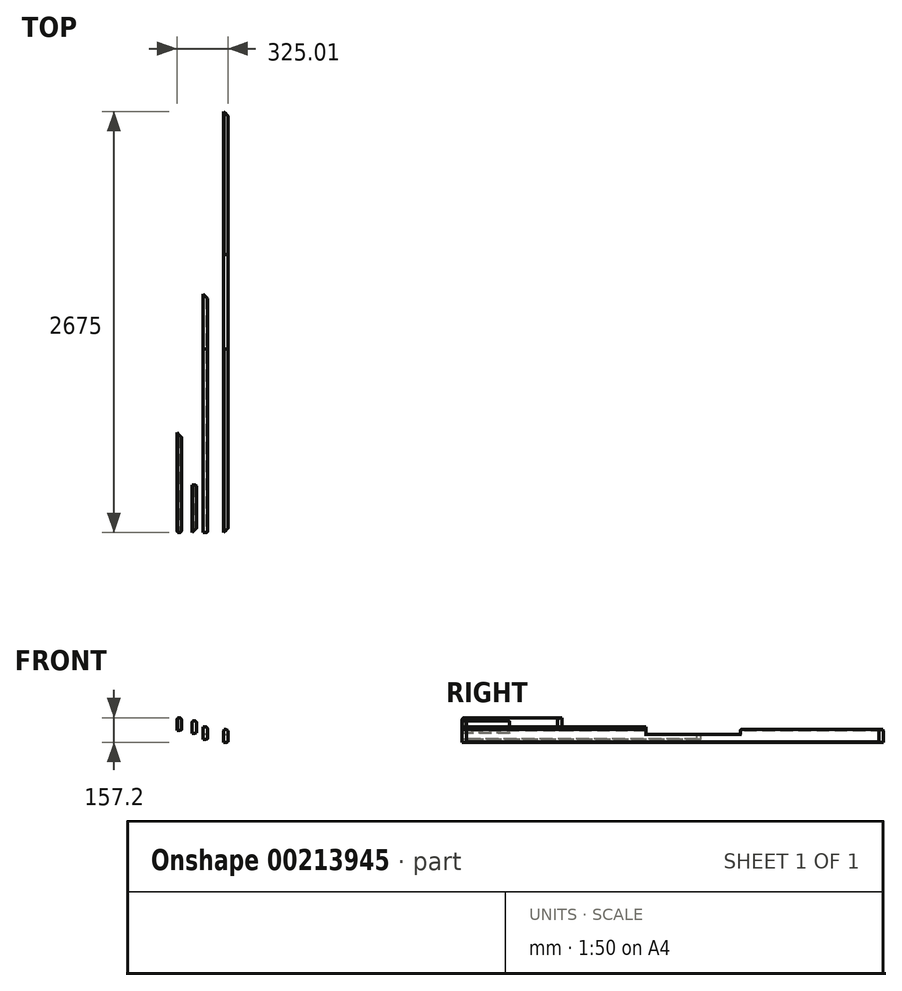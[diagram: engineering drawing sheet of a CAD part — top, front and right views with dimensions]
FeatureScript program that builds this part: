
annotation { "Feature Type Name" : "Feature", "Feature Type Description" : "" }
export const myFeature = defineFeature(function(context is Context, id is Id, definition is map)
    precondition{}
    {
        {
            var Q0;
            Q0=qCreatedBy(makeId("Front.planeOp"),FACE);
            var sketch = newSketch(context, id + "F0", { "sketchPlane" : qUnion([Q0])});
            skLineSegment(sketch, "E0.bottom", {"start": v(0, 0) * mm, "end": v(21, 0) * mm});
            skLineSegment(sketch, "E0.top", {"start": v(3, 81.5) * mm, "end": v(14.5, 81.5) * mm});
            skLineSegment(sketch, "E0.left", {"start": v(0, 0) * mm, "end": v(0, 74) * mm});
            skLineSegment(sketch, "E0.right", {"start": v(28.5, 3) * mm, "end": v(28.5, 67.5) * mm});
            skLineSegment(sketch, "E1.top", {"start": v(0, 74) * mm, "end": v(3, 74) * mm});
            skLineSegment(sketch, "E1.right", {"start": v(3, 81.5) * mm, "end": v(3, 74) * mm});
            skLineSegment(sketch, "E2.bottom", {"start": v(28.5, 3) * mm, "end": v(21, 3) * mm});
            skLineSegment(sketch, "E2.right", {"start": v(21, 3) * mm, "end": v(21, 0) * mm});
            skPoint(sketch, "E3.visualSharp", {"position": v(28.5, 81.5) * mm});
            skArc(sketch, "E3.filletArc", {"start": v(28.5, 67.5) * mm, "mid": v(24.4, 77.4) * mm, "end": v(14.5, 81.5) * mm});
            skSolve(sketch);
        }
        {
            var Q0;
            Q0 = qSketchRegion(id + "F0", true);
            extrude(context, id + "F1", {"entities" : qUnion([Q0]), "oppositeDirection" : true, "depth" : 635.4 * mm});
        }
        {
            var Q0;
            Q0=makeQuery(id+"F1.opExtrude","CAP_EDGE",EDGE,{"disambiguationData":[OSD([sQuery(id+"F0.wireOp",EDGE,"E0.top")])],"isStart":true});
            fillet(context, id + "F2", {"entities" : qUnion([Q0]), "radius" : 14 * mm, "tangentPropagation" : true, "allowEdgeOverflow" : false});
        }
        {
            var Q0;
            Q0=makeQuery(id+"F1.opExtrude","SWEPT_FACE",FACE,{"disambiguationData":[OSD([sQuery(id+"F0.wireOp",EDGE,"E0.top")])]});
            var sketch = newSketch(context, id + "F3", { "sketchPlane" : qUnion([Q0])});
            skLineSegment(sketch, "E4.0", {"start": v(0, 635.4) * mm, "end": v(3, 635.4) * mm});
            skLineSegment(sketch, "E5", {"start": v(0, 635.4) * mm, "end": v(32.84, 602.56) * mm});
            skLineSegment(sketch, "E6", {"start": v(32.84, 602.56) * mm, "end": v(32.84, 635.9) * mm});
            skLineSegment(sketch, "E7", {"start": v(32.84, 635.9) * mm, "end": v(0, 635.4) * mm});
            skLineSegment(sketch, "E8.bottom", {"start": v(-8.71, 7.5) * mm, "end": v(3, 7.5) * mm});
            skLineSegment(sketch, "E8.top", {"start": v(-8.71, -8.39) * mm, "end": v(3, -8.39) * mm});
            skLineSegment(sketch, "E8.left", {"start": v(-8.71, 7.5) * mm, "end": v(-8.71, -8.39) * mm});
            skLineSegment(sketch, "E8.right", {"start": v(3, 7.5) * mm, "end": v(3, -8.39) * mm});
            skSolve(sketch);
        }
        {
            var Q0;
            Q0 = qSketchRegion(id + "F3", true);
            extrude(context, id + "F4", {"entities" : qUnion([Q0]), "operationType" : NewBodyOperationType.REMOVE, "endBound" : BoundingType.THROUGH_ALL, "oppositeDirection" : true, "depth" : 25 * mm});
        }
        {
            var Q0;
            Q0=qCreatedBy(makeId("Front.planeOp"),FACE);
            var sketch = newSketch(context, id + "F5", { "sketchPlane" : qUnion([Q0])});
            skLineSegment(sketch, "E9.bottom", {"start": v(95.79, -19.15) * mm, "end": v(116.79, -19.15) * mm});
            skLineSegment(sketch, "E9.top", {"start": v(98.79, 62.35) * mm, "end": v(110.29, 62.35) * mm});
            skLineSegment(sketch, "E9.left", {"start": v(95.79, -19.15) * mm, "end": v(95.79, 54.85) * mm});
            skLineSegment(sketch, "E9.right", {"start": v(124.29, -16.15) * mm, "end": v(124.29, 48.35) * mm});
            skLineSegment(sketch, "E10.top", {"start": v(95.79, 54.85) * mm, "end": v(98.79, 54.85) * mm});
            skLineSegment(sketch, "E10.right", {"start": v(98.79, 62.35) * mm, "end": v(98.79, 54.85) * mm});
            skLineSegment(sketch, "E11.bottom", {"start": v(124.29, -16.15) * mm, "end": v(116.79, -16.15) * mm});
            skLineSegment(sketch, "E11.right", {"start": v(116.79, -16.15) * mm, "end": v(116.79, -19.15) * mm});
            skArc(sketch, "E12.filletArc", {"start": v(124.29, 48.35) * mm, "mid": v(120.18, 58.25) * mm, "end": v(110.29, 62.35) * mm});
            skSolve(sketch);
        }
        {
            var Q0;
            Q0 = qSketchRegion(id + "F5", true);
            extrude(context, id + "F6", {"entities" : qUnion([Q0]), "oppositeDirection" : true, "depth" : 301.5 * mm});
        }
        {
            var Q0;
            Q0=makeQuery(id+"F6.opExtrude","SWEPT_FACE",FACE,{"disambiguationData":[OSD([sQuery(id+"F5.wireOp",EDGE,"E9.top")])]});
            var sketch = newSketch(context, id + "F7", { "sketchPlane" : qUnion([Q0])});
            skLineSegment(sketch, "E13", {"start": v(95.8, 0) * mm, "end": v(128.08, 32.3) * mm});
            skLineSegment(sketch, "E14", {"start": v(128.08, 32.3) * mm, "end": v(128.08, -11.5) * mm});
            skLineSegment(sketch, "E15", {"start": v(128.08, -11.5) * mm, "end": v(95.8, 0) * mm});
            skSolve(sketch);
        }
        {
            var Q0;
            Q0 = qSketchRegion(id + "F7", true);
            extrude(context, id + "F8", {"entities" : qUnion([Q0]), "operationType" : NewBodyOperationType.REMOVE, "endBound" : BoundingType.THROUGH_ALL, "oppositeDirection" : true, "depth" : 25 * mm});
        }
        {
            var Q0;
            Q0=makeQuery(id+"F6.opExtrude","CAP_EDGE",EDGE,{"disambiguationData":[OSD([sQuery(id+"F5.wireOp",EDGE,"E9.right")])],"isStart":false});
            fillet(context, id + "F9", {"entities" : qUnion([Q0]), "radius" : 7 * mm, "tangentPropagation" : true, "allowEdgeOverflow" : false});
        }
        {
            var Q0;
            Q0=qCreatedBy(makeId("Front.planeOp"),FACE);
            var sketch = newSketch(context, id + "F10", { "sketchPlane" : qUnion([Q0])});
            skLineSegment(sketch, "E16.bottom", {"start": v(164.93, -57.23) * mm, "end": v(185.93, -57.23) * mm});
            skLineSegment(sketch, "E16.top", {"start": v(167.93, 24.27) * mm, "end": v(179.43, 24.27) * mm});
            skLineSegment(sketch, "E16.left", {"start": v(164.93, -57.23) * mm, "end": v(164.93, 16.77) * mm});
            skLineSegment(sketch, "E16.right", {"start": v(193.43, -54.23) * mm, "end": v(193.43, 10.27) * mm});
            skLineSegment(sketch, "E17.top", {"start": v(164.93, 16.77) * mm, "end": v(167.93, 16.77) * mm});
            skLineSegment(sketch, "E17.right", {"start": v(167.93, 24.27) * mm, "end": v(167.93, 16.77) * mm});
            skLineSegment(sketch, "E18.bottom", {"start": v(193.43, -54.23) * mm, "end": v(185.93, -54.23) * mm});
            skLineSegment(sketch, "E18.right", {"start": v(185.93, -54.23) * mm, "end": v(185.93, -57.23) * mm});
            skPoint(sketch, "E19.visualSharp", {"position": v(193.43, 24.27) * mm});
            skArc(sketch, "E19.filletArc", {"start": v(193.43, 10.27) * mm, "mid": v(189.33, 20.17) * mm, "end": v(179.43, 24.27) * mm});
            skSolve(sketch);
        }
        {
            var Q0;
            Q0 = qSketchRegion(id + "F10", true);
            extrude(context, id + "F11", {"entities" : qUnion([Q0]), "oppositeDirection" : true, "depth" : (908.12 + 608) * mm});
        }
        {
            var Q0;
            Q0=makeQuery(id+"F11.opExtrude","SWEPT_FACE",FACE,{"disambiguationData":[OSD([sQuery(id+"F10.wireOp",EDGE,"E16.top")])]});
            var sketch = newSketch(context, id + "F12", { "sketchPlane" : qUnion([Q0])});
            skLineSegment(sketch, "E20", {"start": v(164.93, 1516.12) * mm, "end": v(222.4, 1458.65) * mm});
            skLineSegment(sketch, "E21", {"start": v(222.4, 1458.65) * mm, "end": v(222.4, 1522.96) * mm});
            skLineSegment(sketch, "E22", {"start": v(222.4, 1522.96) * mm, "end": v(164.93, 1516.12) * mm});
            skPoint(sketch, "E23.0.end.orphan", {"position": v(167.93, 1516.12) * mm});
            skSolve(sketch);
        }
        {
            var Q0;
            Q0 = qSketchRegion(id + "F12", true);
            extrude(context, id + "F13", {"entities" : qUnion([Q0]), "operationType" : NewBodyOperationType.REMOVE, "endBound" : BoundingType.THROUGH_ALL, "oppositeDirection" : true, "depth" : 25 * mm});
        }
        {
            var Q0;
            Q0=makeQuery(id+"F11.opExtrude","CAP_EDGE",EDGE,{"disambiguationData":[OSD([sQuery(id+"F10.wireOp",EDGE,"E16.top")])],"isStart":true});
            fillet(context, id + "F14", {"entities" : qUnion([Q0]), "radius" : 7 * mm, "tangentPropagation" : true, "allowEdgeOverflow" : false});
        }
        {
            var Q0;
            Q0=qCreatedBy(makeId("Front.planeOp"),FACE);
            var sketch = newSketch(context, id + "F15", { "sketchPlane" : qUnion([Q0])});
            skLineSegment(sketch, "E24.bottom", {"start": v(296.51, -75.7) * mm, "end": v(317.51, -75.7) * mm});
            skLineSegment(sketch, "E24.top", {"start": v(299.51, 5.8) * mm, "end": v(311.01, 5.8) * mm});
            skLineSegment(sketch, "E24.left", {"start": v(296.51, -75.7) * mm, "end": v(296.51, -1.7) * mm});
            skLineSegment(sketch, "E24.right", {"start": v(325.01, -72.7) * mm, "end": v(325.01, -8.2) * mm});
            skLineSegment(sketch, "E25.top", {"start": v(296.51, -1.7) * mm, "end": v(299.51, -1.7) * mm});
            skLineSegment(sketch, "E25.right", {"start": v(299.51, 5.8) * mm, "end": v(299.51, -1.7) * mm});
            skLineSegment(sketch, "E26.bottom", {"start": v(325.01, -72.7) * mm, "end": v(317.51, -72.7) * mm});
            skLineSegment(sketch, "E26.right", {"start": v(317.51, -72.7) * mm, "end": v(317.51, -75.7) * mm});
            skPoint(sketch, "E27.visualSharp", {"position": v(325.01, 5.8) * mm});
            skArc(sketch, "E27.filletArc", {"start": v(325.01, -8.2) * mm, "mid": v(320.91, 1.7) * mm, "end": v(311.01, 5.8) * mm});
            skSolve(sketch);
        }
        {
            var Q0;
            Q0 = qSketchRegion(id + "F15", true);
            extrude(context, id + "F16", {"entities" : qUnion([Q0]), "oppositeDirection" : true, "depth" : 2675 * mm});
        }
        {
            var Q0;
            Q0=makeQuery(id+"F16.opExtrude","SWEPT_FACE",FACE,{"disambiguationData":[OSD([sQuery(id+"F15.wireOp",EDGE,"E24.top")])]});
            var sketch = newSketch(context, id + "F17", { "sketchPlane" : qUnion([Q0])});
            skLineSegment(sketch, "E28", {"start": v(296.51, 0) * mm, "end": v(325.35, 28.84) * mm});
            skLineSegment(sketch, "E29", {"start": v(325.35, 28.84) * mm, "end": v(328.74, -5.86) * mm});
            skLineSegment(sketch, "E30", {"start": v(328.74, -5.86) * mm, "end": v(296.51, 0) * mm});
            skLineSegment(sketch, "E31", {"start": v(296.51, 2675) * mm, "end": v(329.9, 2641.6) * mm});
            skLineSegment(sketch, "E32", {"start": v(329.9, 2641.6) * mm, "end": v(329.72, 2681.5) * mm});
            skLineSegment(sketch, "E33", {"start": v(329.72, 2681.5) * mm, "end": v(296.51, 2675) * mm});
            skSolve(sketch);
        }
        {
            var Q0;
            Q0 = qSketchRegion(id + "F17", true);
            extrude(context, id + "F18", {"entities" : qUnion([Q0]), "operationType" : NewBodyOperationType.REMOVE, "endBound" : BoundingType.THROUGH_ALL, "oppositeDirection" : true, "depth" : 25 * mm});
        }
        {
            var Q0;
            Q0=makeQuery(id+"F16.opExtrude","SWEPT_FACE",FACE,{"disambiguationData":[OSD([sQuery(id+"F15.wireOp",EDGE,"E24.right")])]});
            var sketch = newSketch(context, id + "F19", { "sketchPlane" : qUnion([Q0])});
            skLineSegment(sketch, "E34.bottom", {"start": v(1766, 77.14) * mm, "end": v(1166, 77.14) * mm});
            skLineSegment(sketch, "E34.top", {"start": v(1766, -25.7) * mm, "end": v(1166, -25.7) * mm});
            skLineSegment(sketch, "E34.left", {"start": v(1766, 77.14) * mm, "end": v(1766, -25.7) * mm});
            skLineSegment(sketch, "E34.right", {"start": v(1166, 77.14) * mm, "end": v(1166, -25.7) * mm});
            skSolve(sketch);
        }
        {
            var Q0;
            Q0 = qSketchRegion(id + "F19", true);
            extrude(context, id + "F20", {"entities" : qUnion([Q0]), "operationType" : NewBodyOperationType.REMOVE, "endBound" : BoundingType.THROUGH_ALL, "oppositeDirection" : true, "depth" : 25 * mm});
        }
        {
            var Q0;
            Q0=makeQuery(id+"F20.boolean.opBoolean","INTERSECT",EDGE,{"derivedFrom":[makeQuery(id+"F16.opExtrude","SWEPT_FACE",FACE,{"disambiguationData":[OSD([sQuery(id+"F15.wireOp",EDGE,"E24.top")])]}),makeQuery(id+"F20.opExtrude","SWEPT_FACE",FACE,{"disambiguationData":[OSD([sQuery(id+"F19.wireOp",EDGE,"E34.right")])]})]});
            var Q1;
            Q1=makeQuery(id+"F20.boolean.opBoolean","COPY",EDGE,{"derivedFrom":makeQuery(id+"F20.opExtrude","CAP_EDGE",EDGE,{"disambiguationData":[OSD([sQuery(id+"F19.wireOp",EDGE,"E34.top")])],"isStart":true})});
            var Q2;
            Q2=makeQuery(id+"F20.boolean.opBoolean","INTERSECT",EDGE,{"derivedFrom":[makeQuery(id+"F16.opExtrude","SWEPT_FACE",FACE,{"disambiguationData":[OSD([sQuery(id+"F15.wireOp",EDGE,"E24.top")])]}),makeQuery(id+"F20.opExtrude","SWEPT_FACE",FACE,{"disambiguationData":[OSD([sQuery(id+"F19.wireOp",EDGE,"E34.left")])]})]});
            fillet(context, id + "F21", {"entities" : qUnion([Q0, Q1, Q2]), "radius" : 7 * mm, "tangentPropagation" : true, "allowEdgeOverflow" : false});
        }
    });
